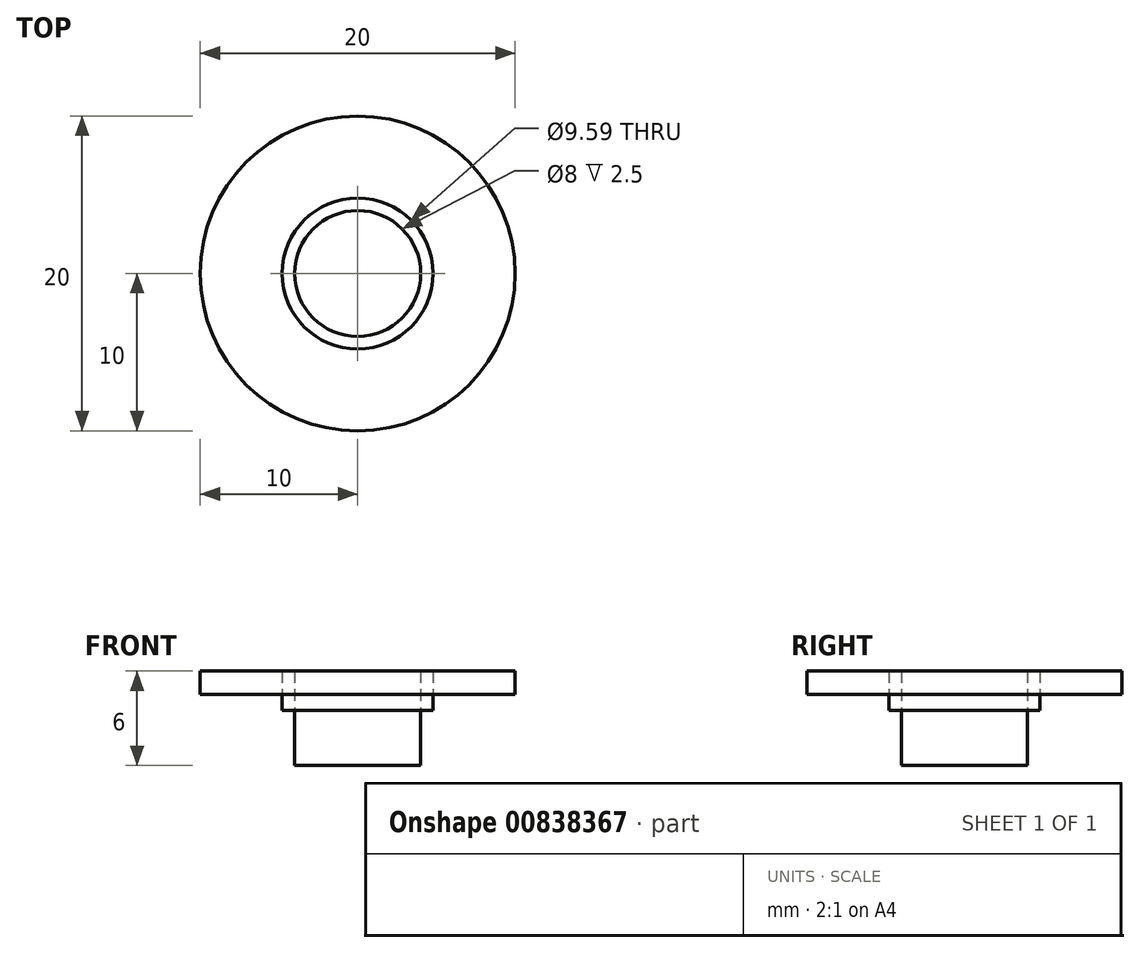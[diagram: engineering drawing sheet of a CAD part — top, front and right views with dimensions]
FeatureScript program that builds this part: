
annotation { "Feature Type Name" : "Feature", "Feature Type Description" : "" }
export const myFeature = defineFeature(function(context is Context, id is Id, definition is map)
    precondition{}
    {
        {
            var Q0;
            Q0=qCreatedBy(makeId("Top.planeOp"),FACE);
            var sketch = newSketch(context, id + "F0", { "sketchPlane" : qUnion([Q0])});
            skCircle(sketch, "E0", {"center": v(0, 0) * mm, "radius": 4 * mm});
            skCircle(sketch, "E1", {"center": v(0, 0) * mm, "radius": 10 * mm});
            skCircle(sketch, "E2", {"center": v(0, 0) * mm, "radius": 4.8 * mm});
            skSolve(sketch);
        }
        {
            var Q0;
            Q0=makeQuery(id+"F0.imprint","IMPRINT",FACE,{"disambiguationData":[TD([[makeQuery(id+"F0.imprint","IMPRINT",EDGE,{"derivedFrom":sQuery(id+"F0.wireOp",EDGE,"E0")}),1.0]])]});
            extrude(context, id + "F1", {"entities" : qUnion([Q0]), "depth" : 6 * mm, "offsetDistance" : 25.4 * mm});
        }
        {
            var Q0;
            Q0=makeQuery(id+"F0.imprint","IMPRINT",FACE,{"disambiguationData":[TD([[makeQuery(id+"F0.imprint","IMPRINT",EDGE,{"derivedFrom":sQuery(id+"F0.wireOp",EDGE,"E1")}),1.0]])]});
            extrude(context, id + "F2", {"entities" : qUnion([Q0]), "depth" : 1.5 * mm, "offsetDistance" : 25.4 * mm});
        }
        {
            var Q0;
            Q0=makeQuery(id+"F2.opExtrude","SWEPT_BODY",BODY,{"disambiguationData":[OSD([sQuery(id+"F0.wireOp",EDGE,"E1"),sQuery(id+"F0.wireOp",EDGE,"E2")])]});
            transform(context, id + "F3", {"entities" : qUnion([Q0]), "transformType" : TransformType.TRANSLATION_3D, "dx" : 0 * mm, "dy" : 0 * mm, "dz" : 4.5 * mm, "makeCopy" : false});
        }
        {
            var Q0;
            Q0=makeQuery(id+"F0.imprint","IMPRINT",FACE,{"disambiguationData":[TD([[makeQuery(id+"F0.imprint","IMPRINT",EDGE,{"derivedFrom":sQuery(id+"F0.wireOp",EDGE,"E0")}),-1.0]])]});
            extrude(context, id + "F4", {"entities" : qUnion([Q0]), "depth" : 2.5 * mm, "offsetDistance" : 25.4 * mm});
        }
        {
            var Q0;
            Q0=makeQuery(id+"F4.opExtrude","SWEPT_BODY",BODY,{"disambiguationData":[OSD([sQuery(id+"F0.wireOp",EDGE,"E0"),sQuery(id+"F0.wireOp",EDGE,"E2")])]});
            transform(context, id + "F5", {"entities" : qUnion([Q0]), "transformType" : TransformType.TRANSLATION_3D, "dx" : 0 * mm, "dy" : 0 * mm, "dz" : 3.5 * mm, "makeCopy" : false});
        }
    });
